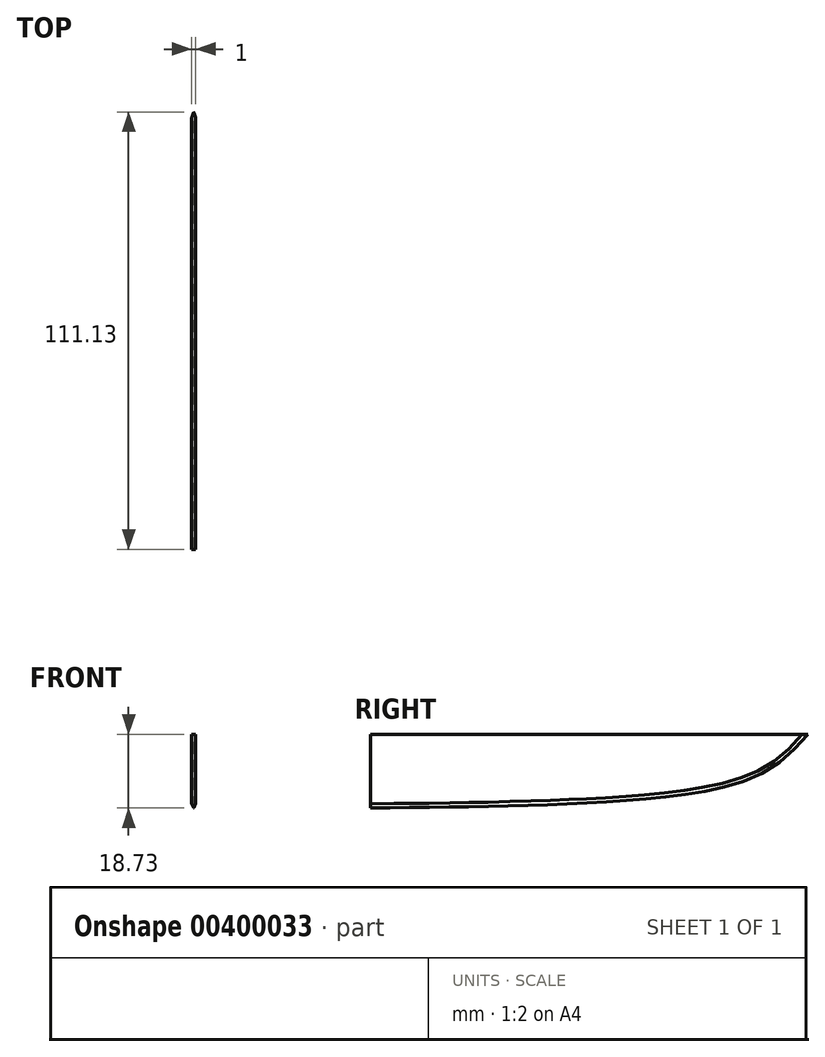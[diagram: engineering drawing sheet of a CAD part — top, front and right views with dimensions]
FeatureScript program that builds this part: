
annotation { "Feature Type Name" : "Feature", "Feature Type Description" : "" }
export const myFeature = defineFeature(function(context is Context, id is Id, definition is map)
    precondition{}
    {
        {
            var Q0;
            Q0=qCreatedBy(makeId("Right.planeOp"),FACE);
            var sketch = newSketch(context, id + "F0", { "sketchPlane" : qUnion([Q0])});
            skLineSegment(sketch, "E0", {"start": v(-34.22, 17.84) * mm, "end": v(78.14, 17.84) * mm});
            skLineSegment(sketch, "E1", {"start": v(-34.22, 17.84) * mm, "end": v(-84.7, 17.84) * mm});
            skLineSegment(sketch, "E2", {"start": v(-84.7, 17.84) * mm, "end": v(-84.7, 5.7) * mm});
            skLineSegment(sketch, "E3", {"start": v(-84.7, 5.7) * mm, "end": v(-34.22, 5.7) * mm});
            skLineSegment(sketch, "E4", {"start": v(-34.22, 5.7) * mm, "end": v(-34.22, -1.82) * mm});
            skFitSpline(sketch, "E5", {"points": [v(-34.22, -1.82) * mm, v(29.6, 0) * mm, v(65.52, 6.92) * mm, v(78.14, 17.84) * mm], "startDerivative": vector(151.37, 1.6) * mm, "endDerivative": vector(46.58, 53.65) * mm});
            skLineSegment(sketch, "E6", {"start": v(-34.22, 17.84) * mm, "end": v(-34.22, 5.7) * mm});
            skSolve(sketch);
        }
        {
            var Q0;
            Q0=makeQuery(id+"F0.imprint","IMPRINT",FACE,{"disambiguationData":[TD([[makeQuery(id+"F0.imprint","IMPRINT",EDGE,{"derivedFrom":sQuery(id+"F0.wireOp",EDGE,"E0")}),-1.0]])]});
            extrude(context, id + "F1", {"entities" : qUnion([Q0]), "endBound" : BoundingType.SYMMETRIC, "depth" : 1 * mm});
        }
        {
            var Q0;
            Q0=makeQuery(id+"F1.opExtrude","CAP_EDGE",EDGE,{"disambiguationData":[OSD([sQuery(id+"F0.wireOp",EDGE,"E5")])],"isStart":false});
            var Q1;
            Q1=makeQuery(id+"F1.opExtrude","CAP_EDGE",EDGE,{"disambiguationData":[OSD([sQuery(id+"F0.wireOp",EDGE,"E5")])],"isStart":true});
            chamfer(context, id + "F2", {"entities" : qUnion([Q0, Q1]), "chamferType" : ChamferType.OFFSET_ANGLE, "width" : 2 * mm, "oppositeDirection" : false, "angle" : 25 * degree, "tangentPropagation" : true});
        }
    });
